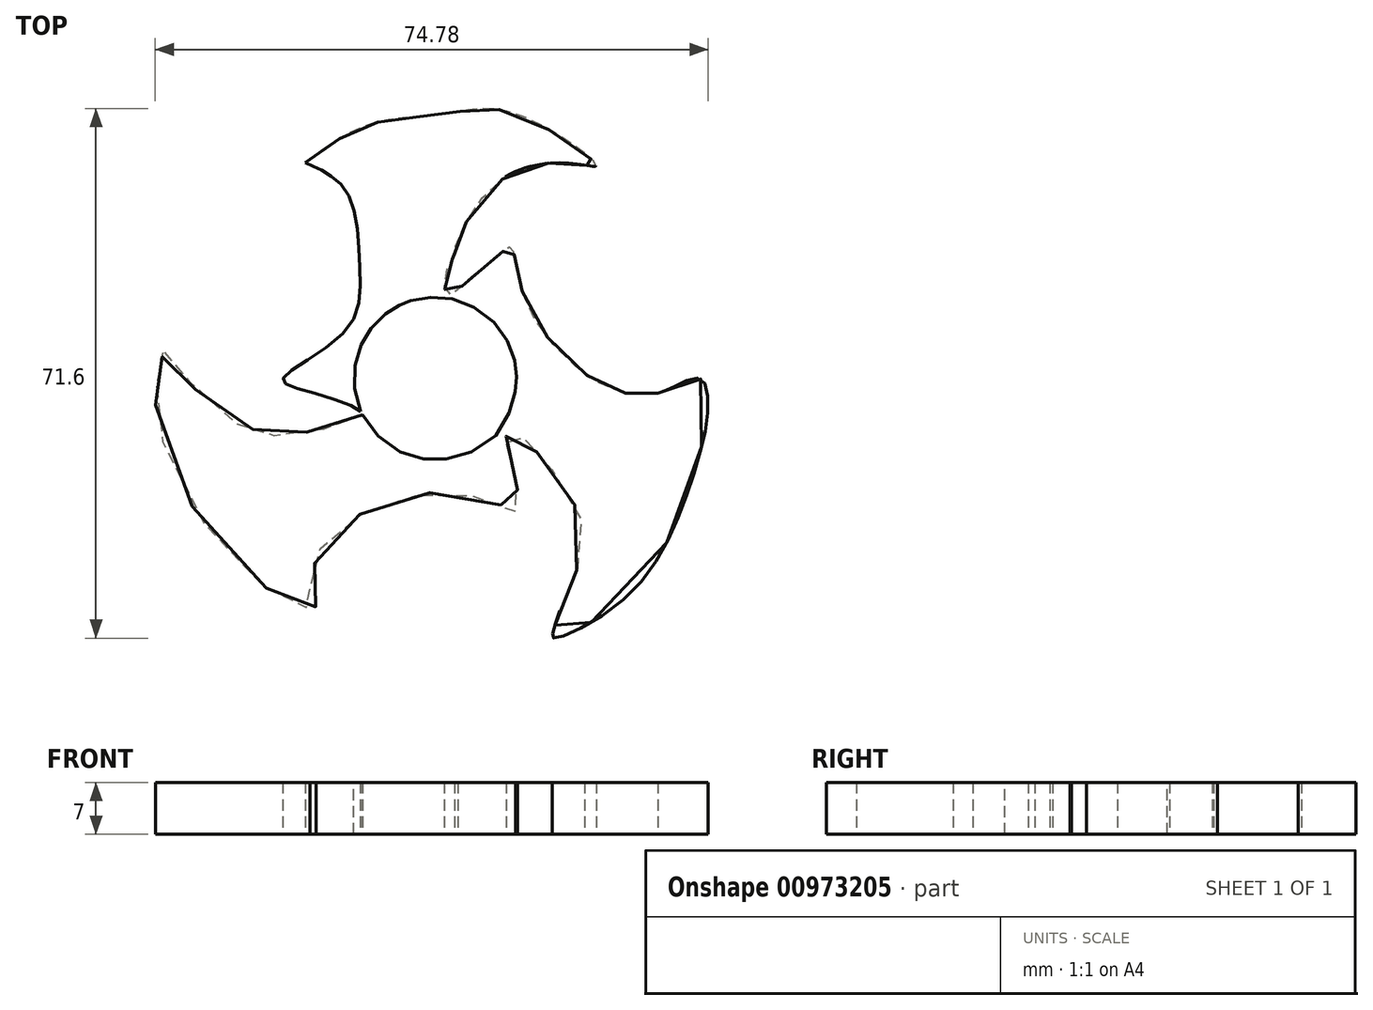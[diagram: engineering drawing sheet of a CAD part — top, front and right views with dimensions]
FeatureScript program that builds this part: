
annotation { "Feature Type Name" : "Feature", "Feature Type Description" : "" }
export const myFeature = defineFeature(function(context is Context, id is Id, definition is map)
    precondition{}
    {
        {
            var Q0;
            Q0=qCreatedBy(makeId("Top.planeOp"),FACE);
            var sketch = newSketch(context, id + "F0", { "sketchPlane" : qUnion([Q0])});
            skFitSpline(sketch, "E0", {"points": [v(-17.54, 29.15) * mm, v(-15.3, 28.11) * mm, v(-11.8, 24.92) * mm, v(-10.2, 15.12) * mm, v(-12.2, 6.35) * mm, v(-20.57, 0) * mm, v(-18.26, -1.46) * mm, v(-10.02, -4.55) * mm, v(-10.29, -5.6) * mm, v(-16.42, -7.12) * mm, v(-21.84, -7.76) * mm, v(-25.2, -6.72) * mm, v(-30.45, -3.85) * mm, v(-36.51, 4.2) * mm, v(-36.75, 4.04) * mm, v(-37.3, 0) * mm, v(-37.79, -1.46) * mm, v(-35.48, -12.46) * mm, v(-23.78, -27.63) * mm, v(-18.08, -30.78) * mm, v(-16.15, -30.88) * mm, v(-16.83, -28.32) * mm, v(-16.4, -25.27) * mm, v(-13.62, -20.4) * mm, v(-5.33, -16.7) * mm, v(0.73, -15.35) * mm, v(8.56, -16.98) * mm, v(10.9, -17.98) * mm, v(10.9, -17.75) * mm, v(11.14, -14.96) * mm, v(10.24, -11.81) * mm, v(9.77, -7.16) * mm, v(10.77, -7.1) * mm, v(13.52, -9.7) * mm, v(16.54, -13.33) * mm, v(20.16, -20.77) * mm, v(19.02, -26.26) * mm, v(17.07, -30.82) * mm, v(15.87, -34.64) * mm, v(16, -35.11) * mm, v(25.65, -29.75) * mm, v(34.03, -15.67) * mm, v(36.91, -3.87) * mm, v(35.7, 0) * mm, v(32.22, -1.2) * mm, v(30.14, -2) * mm], "startDerivative": vector(133.05, -56.3) * mm, "endDerivative": vector(-123.36, -38.15) * mm});
            skFitSpline(sketch, "E1", {"points": [v(30.14, -2) * mm, v(23.44, -1.26) * mm, v(12.45, 9.93) * mm, v(10.52, 17.5) * mm, v(9.99, 17.72) * mm, v(5.14, 13.77) * mm, v(4.72, 13.55) * mm, v(1.96, 11.3) * mm, v(1.53, 14.6) * mm, v(3.05, 17.24) * mm, v(2.72, 17.04) * mm, v(7.82, 25.98) * mm, v(19.4, 28.97) * mm, v(21.77, 28.82) * mm, v(10.94, 35.77) * mm, v(1.36, 35.77) * mm, v(-8.95, 34.3) * mm, v(-17.54, 29.15) * mm], "startDerivative": vector(-97.58, -9.1) * mm, "endDerivative": vector(-103.76, -79.6) * mm});
            skFitSpline(sketch, "E2", {"points": [v(-4.26, 10.14) * mm, v(-4.98, 9.8) * mm, v(-6.56, 8.83) * mm, v(-8.74, 6.68) * mm, v(-10.02, 4.55) * mm, v(-10.92, 1.34) * mm, v(-10.7, -2.55) * mm, v(-8.91, -6.44) * mm, v(-4.97, -9.81) * mm, v(-0.88, -10.96) * mm, v(2.81, -10.63) * mm, v(7.93, -8) * mm, v(10.3, -3.85) * mm, v(10.94, -1.14) * mm, v(11, 0.3) * mm, v(10.78, 2.17) * mm, v(9.77, 5.06) * mm, v(7.57, 7.98) * mm, v(3.75, 10.34) * mm, v(0.5, 10.99) * mm, v(-2.78, 10.64) * mm, v(-4.26, 10.14) * mm]});
            skSolve(sketch);
        }
        {
            var Q0;
            {var subQ0=sQuery(id+"F0.wireOp",EDGE,"E1");Q0=makeQuery(id+"F0.imprint","IMPRINT",FACE,{"disambiguationData":[TD([[makeQuery(id+"F0.imprint","IMPRINT",EDGE,{"derivedFrom":subQ0}),1.0]])]});}
            extrude(context, id + "F1", {"entities" : qUnion([Q0]), "depth" : 7 * mm, "offsetDistance" : 25.4 * mm});
        }
    });
